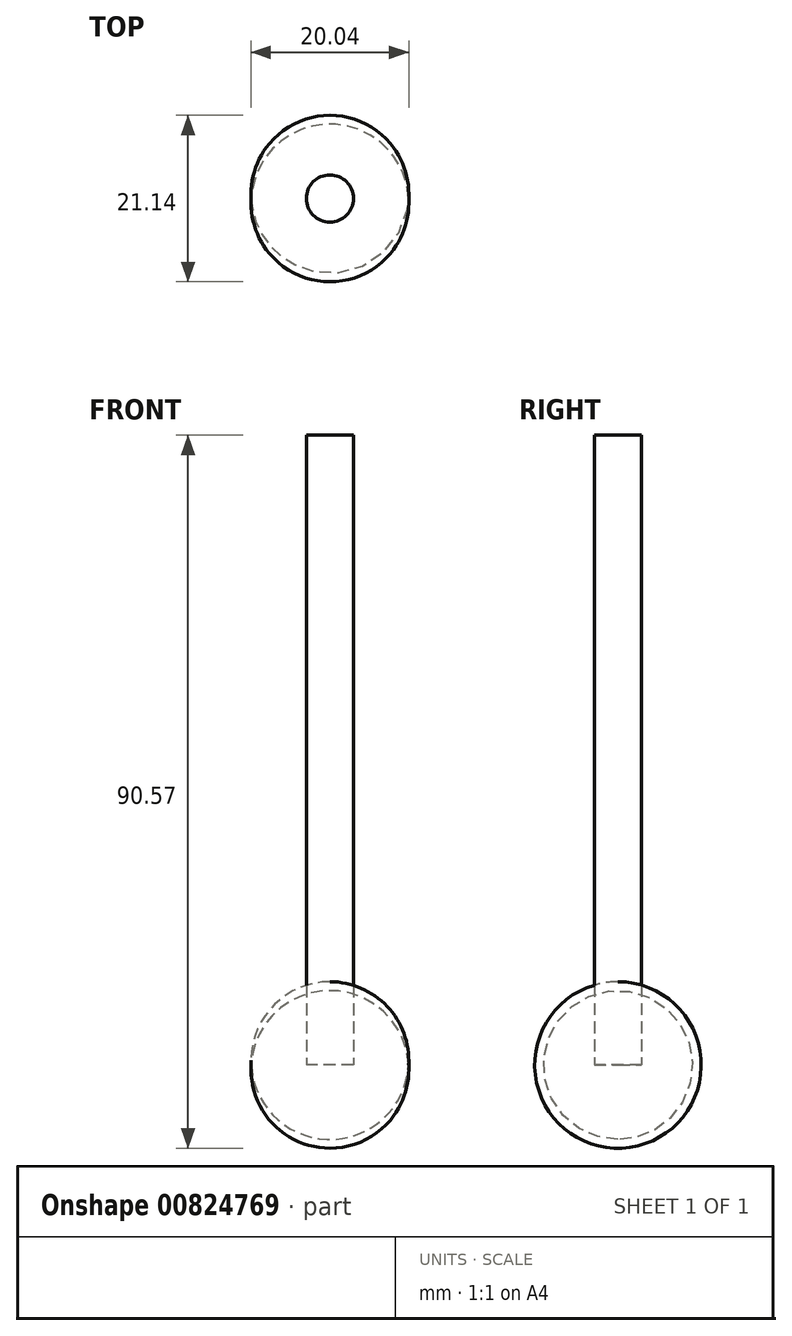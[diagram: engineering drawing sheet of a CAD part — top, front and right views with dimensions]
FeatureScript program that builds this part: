
annotation { "Feature Type Name" : "Feature", "Feature Type Description" : "" }
export const myFeature = defineFeature(function(context is Context, id is Id, definition is map)
    precondition{}
    {
        {
            var Q0;
            Q0=qCreatedBy(makeId("Top.planeOp"),FACE);
            var sketch = newSketch(context, id + "F0", { "sketchPlane" : qUnion([Q0])});
            skCircle(sketch, "E0", {"center": v(0, 0) * mm, "radius": 3 * mm});
            skSolve(sketch);
        }
        {
            var Q0;
            Q0 = qSketchRegion(id + "F0", true);
            extrude(context, id + "F1", {"entities" : qUnion([Q0]), "depth" : 80 * mm, "offsetDistance" : 25 * mm});
        }
        {
            var Q0;
            Q0=qCreatedBy(makeId("Top.planeOp"),FACE);
            var sketch = newSketch(context, id + "F2", { "sketchPlane" : qUnion([Q0])});
            skLineSegment(sketch, "E1", {"start": v(0, 0) * mm, "end": v(10, 0) * mm});
            skLineSegment(sketch, "E2", {"start": v(0, 0) * mm, "end": v(-10, 0) * mm});
            skArc(sketch, "E3", {"start": v(-10, 0) * mm, "mid": v(0, -10.57) * mm, "end": v(10, 0) * mm});
            skSolve(sketch);
        }
        {
            var Q0;
            Q0=makeQuery(id+"F2.imprint","IMPRINT",FACE,{"disambiguationData":[TD([[makeQuery(id+"F2.imprint","IMPRINT",EDGE,{"derivedFrom":sQuery(id+"F2.wireOp",EDGE,"E1")}),-1.0]])]});
            var Q1;
            Q1=sQuery(id+"F2.wireOp",EDGE,"E1");
            revolve(context, id + "F3", {"surfaceOperationType" : NewSurfaceOperationType.NEW, "entities" : qUnion([Q0]), "axis" : qUnion([Q1]), "revolveType" : RevolveType.SYMMETRIC, "angle" : 360 * degree});
        }
    });
